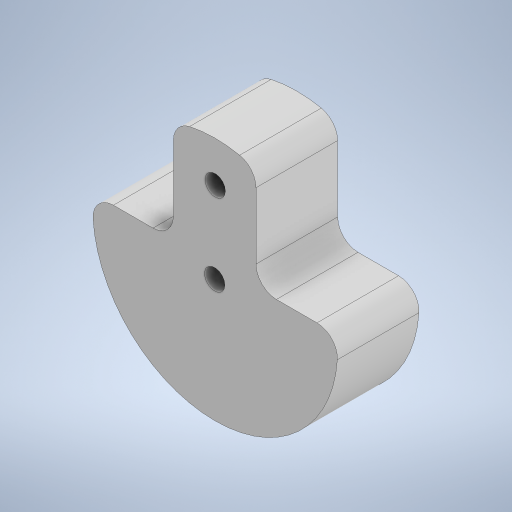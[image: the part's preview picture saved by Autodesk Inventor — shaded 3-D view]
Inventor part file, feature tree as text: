
AUTODESK INVENTOR PART (.ipt)
format: ipt  version: 2023 (Build 270158000, 158)  size: 253,952 bytes
history: native  units: in
note: dims shown in document units (in); Inventor stores cm internally (conversion verified against a paired STEP export)
features: extrude x1, sketch x1
ambient origin geometry x8: Origin, YZ Plane, XZ Plane, XY Plane, X Axis, Y Axis, Z Axis, Center Point
bodies: Solid1 (feature_tree)
feature tree (2):
  extrude  "Extrusion1"  Depth=0.125in
  sketch  "Sketch1"  dims[d2=1.5in d3=0.125in d6=0.125in d7=0.5in d8=0.0in d11=0.625in d12=0.125in d10=0.5in d13=0.0344in]
